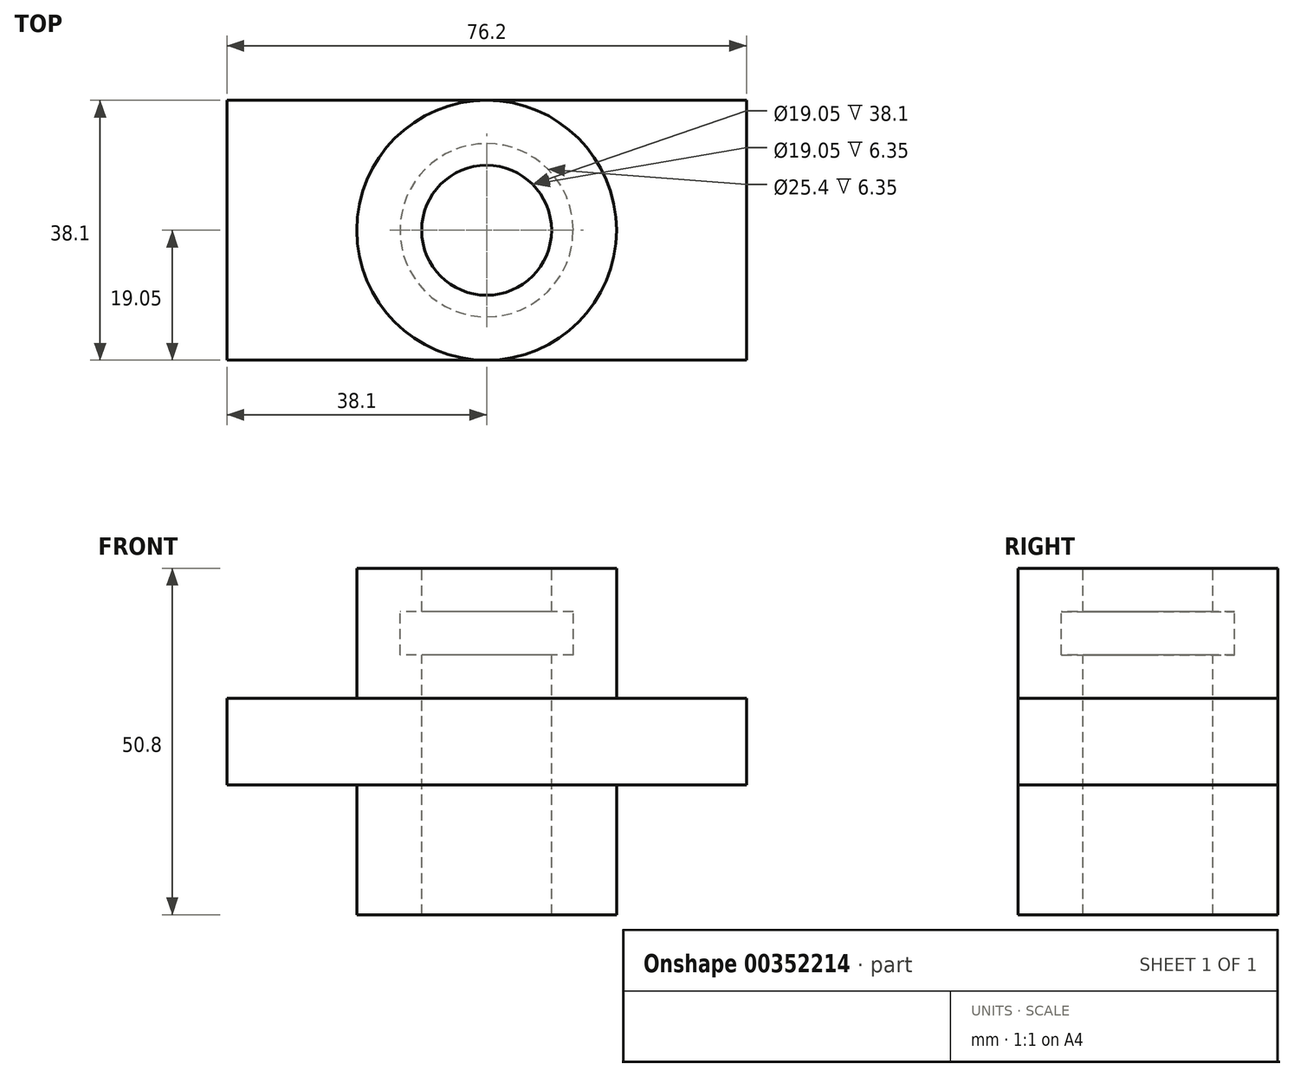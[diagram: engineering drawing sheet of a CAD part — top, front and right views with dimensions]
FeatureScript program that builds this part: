
annotation { "Feature Type Name" : "Feature", "Feature Type Description" : "" }
export const myFeature = defineFeature(function(context is Context, id is Id, definition is map)
    precondition{}
    {
        {
            var Q0;
            Q0=qCreatedBy(makeId("Front.planeOp"),FACE);
            var sketch = newSketch(context, id + "F0", { "sketchPlane" : qUnion([Q0])});
            skLineSegment(sketch, "E0.bottom", {"start": v(0, 0) * mm, "end": v(76.2, 0) * mm});
            skLineSegment(sketch, "E0.top", {"start": v(0, 12.7) * mm, "end": v(76.2, 12.7) * mm});
            skLineSegment(sketch, "E0.left", {"start": v(0, 0) * mm, "end": v(0, 12.7) * mm});
            skLineSegment(sketch, "E0.right", {"start": v(76.2, 0) * mm, "end": v(76.2, 12.7) * mm});
            skSolve(sketch);
        }
        {
            var Q0;
            Q0 = qSketchRegion(id + "F0", true);
            extrude(context, id + "F1", {"entities" : qUnion([Q0]), "endBound" : BoundingType.SYMMETRIC, "depth" : 38.1 * mm});
        }
        {
            var Q0;
            Q0=makeQuery(id+"F1.opExtrude","SWEPT_FACE",FACE,{"disambiguationData":[OSD([sQuery(id+"F0.wireOp",EDGE,"E0.top")])]});
            var sketch = newSketch(context, id + "F2", { "sketchPlane" : qUnion([Q0])});
            skCircle(sketch, "E1", {"center": v(38.1, 0) * mm, "radius": 19.05 * mm});
            skPoint(sketch, "E1.centerSnap0", {"position": v(0, 0) * mm});
            skSolve(sketch);
        }
        {
            var Q0;
            Q0 = qSketchRegion(id + "F2", true);
            extrude(context, id + "F3", {"entities" : qUnion([Q0]), "operationType" : NewBodyOperationType.ADD, "depth" : 19.05 * mm, "hasSecondDirection" : true, "secondDirectionOppositeDirection" : true, "secondDirectionDepth" : 31.75 * mm});
        }
        {
            var Q0;
            Q0=qCreatedBy(makeId("Top.planeOp"),FACE);
            var sketch = newSketch(context, id + "F4", { "sketchPlane" : qUnion([Q0])});
            skCircle(sketch, "E2", {"center": v(38.1, 0) * mm, "radius": 9.53 * mm});
            skSolve(sketch);
        }
        {
            var Q0;
            Q0 = qSketchRegion(id + "F4", true);
            extrude(context, id + "F5", {"entities" : qUnion([Q0]), "operationType" : NewBodyOperationType.REMOVE, "endBound" : BoundingType.THROUGH_ALL, "oppositeDirection" : true, "depth" : 25.4 * mm, "hasSecondDirection" : true, "secondDirectionBound" : SecondDirectionBoundingType.THROUGH_ALL, "secondDirectionOppositeDirection" : false, "secondDirectionDepth" : 25.4 * mm});
        }
        {
            var Q0;
            Q0=makeQuery(id+"F3.opExtrude","CAP_FACE",FACE,{"disambiguationData":[OSD([sQuery(id+"F2.wireOp",EDGE,"E1")])],"isStart":false});
            var sketch = newSketch(context, id + "F6", { "sketchPlane" : qUnion([Q0])});
            skCircle(sketch, "E3", {"center": v(38.1, 0) * mm, "radius": 12.7 * mm});
            skSolve(sketch);
        }
        {
            var Q0;
            Q0 = qSketchRegion(id + "F6", true);
            extrude(context, id + "F7", {"entities" : qUnion([Q0]), "operationType" : NewBodyOperationType.REMOVE, "oppositeDirection" : true, "depth" : 12.7 * mm, "hasSecondDirection" : true, "secondDirectionOppositeDirection" : true, "secondDirectionDepth" : 6.35 * mm});
        }
    });
